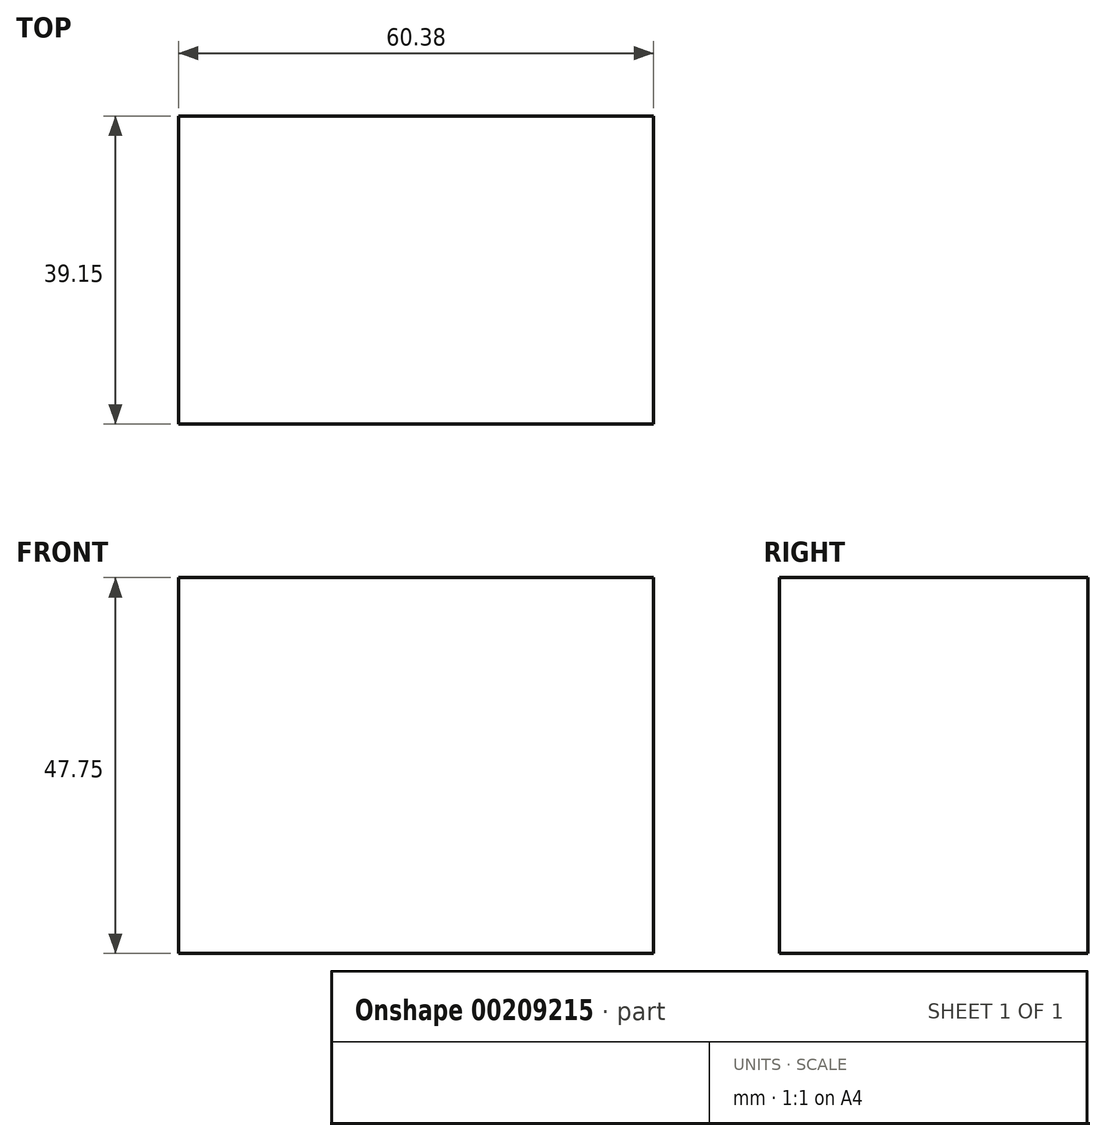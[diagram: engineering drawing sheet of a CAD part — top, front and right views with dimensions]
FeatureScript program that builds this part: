
annotation { "Feature Type Name" : "Feature", "Feature Type Description" : "" }
export const myFeature = defineFeature(function(context is Context, id is Id, definition is map)
    precondition{}
    {
        {
            var Q0;
            Q0=qCreatedBy(makeId("Top.planeOp"),FACE);
            var sketch = newSketch(context, id + "F0", { "sketchPlane" : qUnion([Q0])});
            skLineSegment(sketch, "E0.bottom", {"start": v(-60.38, 39.15) * mm, "end": v(0, 39.15) * mm});
            skLineSegment(sketch, "E0.top", {"start": v(-60.38, 0) * mm, "end": v(0, 0) * mm});
            skLineSegment(sketch, "E0.left", {"start": v(-60.38, 39.15) * mm, "end": v(-60.38, 0) * mm});
            skLineSegment(sketch, "E0.right", {"start": v(0, 39.15) * mm, "end": v(0, 0) * mm});
            skSolve(sketch);
        }
        {
            var Q0;
            Q0=makeQuery(id+"F0.imprint","IMPRINT",FACE,{"disambiguationData":[TD([[makeQuery(id+"F0.imprint","IMPRINT",EDGE,{"derivedFrom":sQuery(id+"F0.wireOp",EDGE,"E0.bottom")}),-1.0]])]});
            extrude(context, id + "F1", {"entities" : qUnion([Q0]), "oppositeDirection" : true, "depth" : 47.75 * mm});
        }
    });
